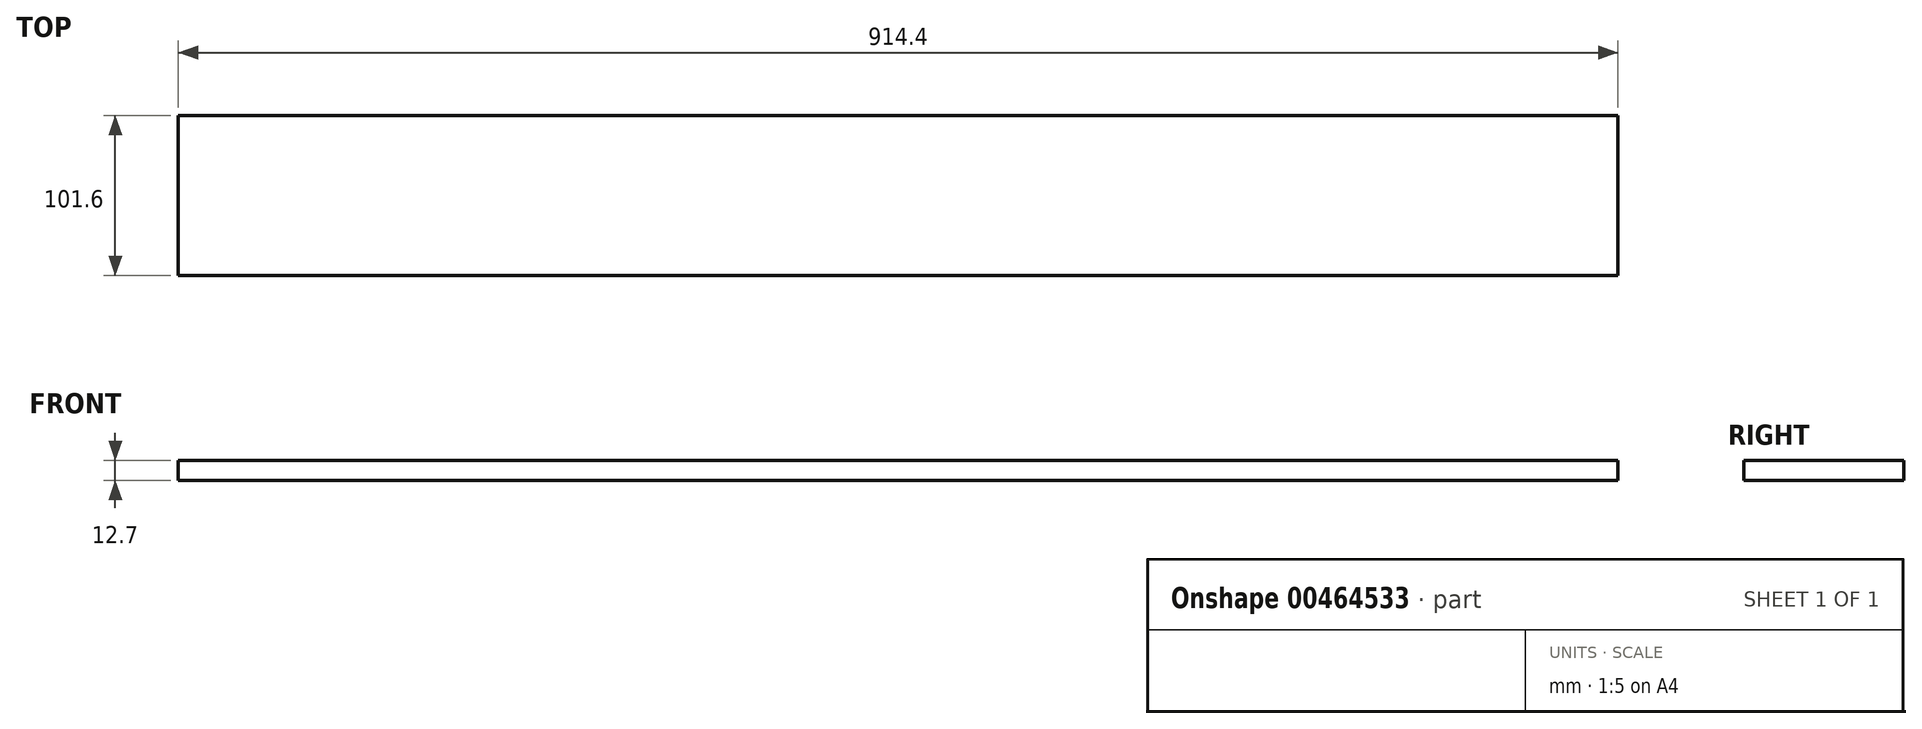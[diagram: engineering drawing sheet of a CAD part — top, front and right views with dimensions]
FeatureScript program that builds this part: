
annotation { "Feature Type Name" : "Feature", "Feature Type Description" : "" }
export const myFeature = defineFeature(function(context is Context, id is Id, definition is map)
    precondition{}
    {
        {
            var Q0;
            Q0=qCreatedBy(makeId("Top.planeOp"),FACE);
            var sketch = newSketch(context, id + "F0", { "sketchPlane" : qUnion([Q0])});
            skLineSegment(sketch, "E0.bottom", {"start": v(457.2, -50.8) * mm, "end": v(-457.2, -50.8) * mm});
            skLineSegment(sketch, "E0.top", {"start": v(457.2, 50.8) * mm, "end": v(-457.2, 50.8) * mm});
            skLineSegment(sketch, "E0.left", {"start": v(457.2, -50.8) * mm, "end": v(457.2, 50.8) * mm});
            skLineSegment(sketch, "E0.right", {"start": v(-457.2, -50.8) * mm, "end": v(-457.2, 50.8) * mm});
            skPoint(sketch, "E0.middle", {"position": v(0, 0) * mm});
            skSolve(sketch);
        }
        {
            var Q0;
            Q0 = qSketchRegion(id + "F0", true);
            extrude(context, id + "F1", {"entities" : qUnion([Q0]), "depth" : 12.7 * mm});
        }
    });
